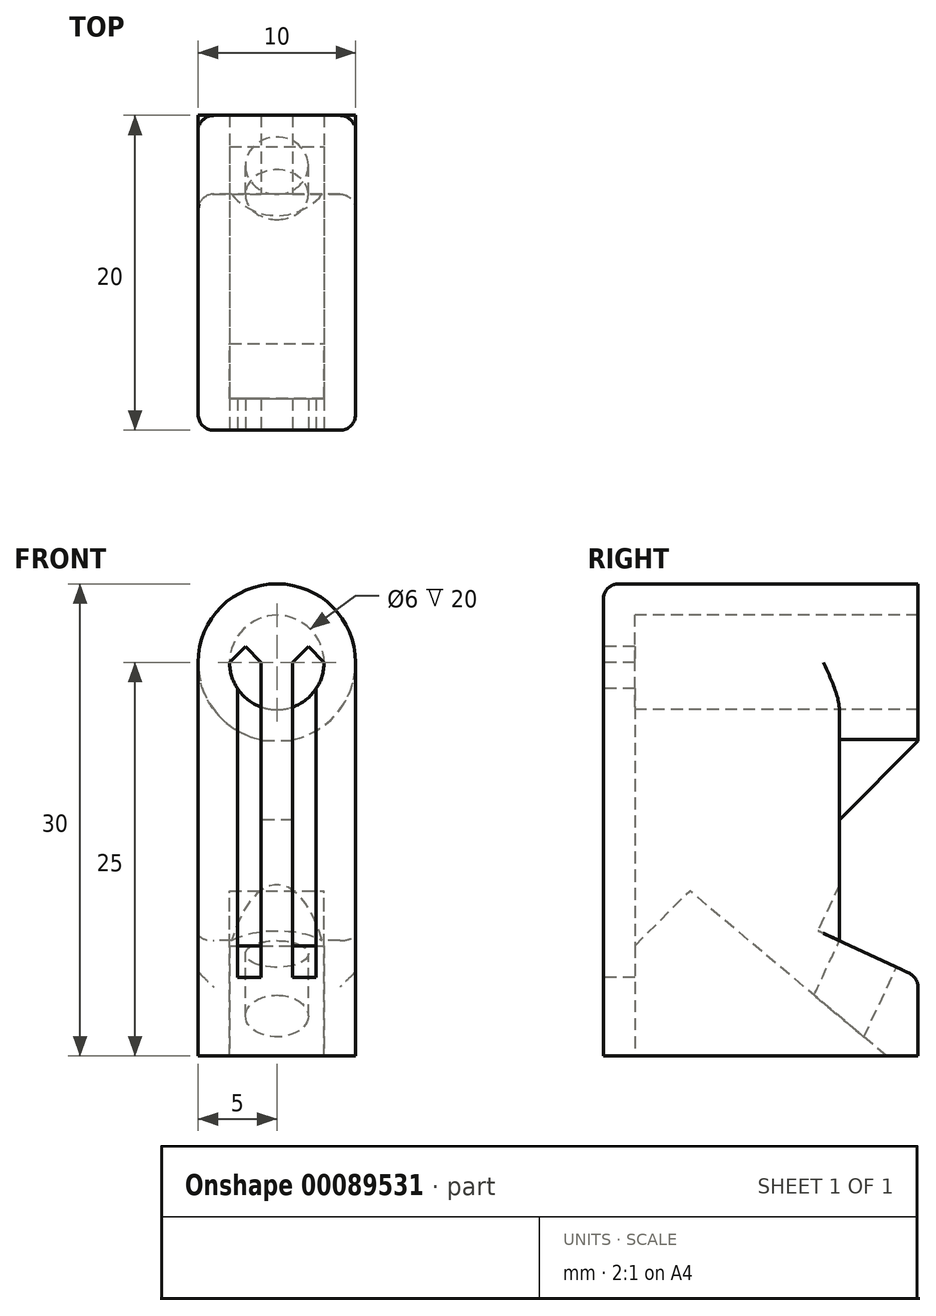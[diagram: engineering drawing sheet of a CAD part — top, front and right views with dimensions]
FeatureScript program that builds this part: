
annotation { "Feature Type Name" : "Feature", "Feature Type Description" : "" }
export const myFeature = defineFeature(function(context is Context, id is Id, definition is map)
    precondition{}
    {
        {
            var Q0;
            Q0=qCreatedBy(makeId("Top.planeOp"),FACE);
            var sketch = newSketch(context, id + "F0", { "sketchPlane" : qUnion([Q0])});
            skLineSegment(sketch, "E0.top", {"start": v(5, 12.5) * mm, "end": v(-5, 12.5) * mm});
            skLineSegment(sketch, "E0.left", {"start": v(5, 7.5) * mm, "end": v(5, 12.5) * mm});
            skLineSegment(sketch, "E0.right", {"start": v(-5, 7.5) * mm, "end": v(-5, 12.5) * mm});
            skLineSegment(sketch, "E1.bottom", {"start": v(5, -7.5) * mm, "end": v(-5, -7.5) * mm});
            skLineSegment(sketch, "E1.top", {"start": v(5, 7.5) * mm, "end": v(-5, 7.5) * mm});
            skLineSegment(sketch, "E1.left", {"start": v(5, -7.5) * mm, "end": v(5, 7.5) * mm});
            skLineSegment(sketch, "E1.right", {"start": v(-5, -7.5) * mm, "end": v(-5, 7.5) * mm});
            skSolve(sketch);
        }
        {
            var Q0;
            Q0=makeQuery(id+"F0.imprint","IMPRINT",FACE,{"disambiguationData":[TD([[makeQuery(id+"F0.imprint","IMPRINT",EDGE,{"derivedFrom":sQuery(id+"F0.wireOp",EDGE,"E1.bottom")}),-1.0]])]});
            extrude(context, id + "F1", {"entities" : qUnion([Q0]), "depth" : 30 * mm});
        }
        {
            var Q0;
            Q0 = qSketchRegion(id + "F0", true);
            extrude(context, id + "F2", {"entities" : qUnion([Q0]), "operationType" : NewBodyOperationType.ADD, "depth" : 5 * mm});
        }
        {
            var Q0;
            Q0=makeQuery(id+"F1.opExtrude","SWEPT_FACE",FACE,{"disambiguationData":[OSD([sQuery(id+"F0.wireOp",EDGE,"E1.bottom")])]});
            var sketch = newSketch(context, id + "F3", { "sketchPlane" : qUnion([Q0])});
            skCircle(sketch, "E2", {"center": v(0, 25) * mm, "radius": 3 * mm});
            skSolve(sketch);
        }
        {
            var Q0;
            Q0 = qSketchRegion(id + "F3", true);
            extrude(context, id + "F4", {"entities" : qUnion([Q0]), "operationType" : NewBodyOperationType.REMOVE, "endBound" : BoundingType.THROUGH_ALL, "oppositeDirection" : true, "depth" : 25 * mm});
        }
        {
            var Q0;
            Q0=makeQuery(id+"F1.opExtrude","SWEPT_FACE",FACE,{"disambiguationData":[OSD([sQuery(id+"F0.wireOp",EDGE,"E1.bottom")])]});
            var sketch = newSketch(context, id + "F5", { "sketchPlane" : qUnion([Q0])});
            skCircle(sketch, "E3.0", {"center": v(0, 25) * mm, "radius": 3 * mm});
            skLineSegment(sketch, "E4", {"start": v(-2.83, 26) * mm, "end": v(2.83, 26) * mm});
            skSolve(sketch);
        }
        {
            var Q0;
            {var subQ0=sQuery(id+"F5.wireOp",EDGE,"E4");Q0=makeQuery(id+"F5.imprint","IMPRINT",FACE,{"disambiguationData":[TD([[makeQuery(id+"F5.imprint","IMPRINT",EDGE,{"derivedFrom":subQ0}),1.0]])]});}
            extrude(context, id + "F6", {"entities" : qUnion([Q0]), "operationType" : NewBodyOperationType.ADD, "oppositeDirection" : true, "depth" : 2 * mm});
        }
        {
            var Q0;
            Q0=makeQuery(id+"F2.opExtrude","CAP_FACE",FACE,{"disambiguationData":[OSD([sQuery(id+"F0.wireOp",EDGE,"E0.bottom"),sQuery(id+"F0.wireOp",EDGE,"E0.top"),sQuery(id+"F0.wireOp",EDGE,"E0.left"),sQuery(id+"F0.wireOp",EDGE,"E0.right"),sQuery(id+"F0.wireOp",EDGE,"E1.bottom"),sQuery(id+"F0.wireOp",EDGE,"E1.top"),sQuery(id+"F0.wireOp",EDGE,"E1.left"),sQuery(id+"F0.wireOp",EDGE,"E1.right")])],"isStart":false});
            var sketch = newSketch(context, id + "F7", { "sketchPlane" : qUnion([Q0])});
            skLineSegment(sketch, "E5.bottom", {"start": v(-1, -7.5) * mm, "end": v(-2.5, -7.5) * mm});
            skLineSegment(sketch, "E5.top", {"start": v(-1, -5.5) * mm, "end": v(-2.5, -5.5) * mm});
            skLineSegment(sketch, "E5.left", {"start": v(-1, -7.5) * mm, "end": v(-1, -5.5) * mm});
            skLineSegment(sketch, "E5.right", {"start": v(-2.5, -7.5) * mm, "end": v(-2.5, -5.5) * mm});
            skPoint(sketch, "E5.middle", {"position": v(-1.75, -6.5) * mm});
            skLineSegment(sketch, "E6.bottom", {"start": v(2.5, -5.5) * mm, "end": v(1, -5.5) * mm});
            skLineSegment(sketch, "E6.top", {"start": v(2.5, -7.5) * mm, "end": v(1, -7.5) * mm});
            skLineSegment(sketch, "E6.left", {"start": v(1, -5.5) * mm, "end": v(1, -7.5) * mm});
            skLineSegment(sketch, "E6.right", {"start": v(2.5, -5.5) * mm, "end": v(2.5, -7.5) * mm});
            skPoint(sketch, "E6.middle", {"position": v(1.75, -6.5) * mm});
            skSolve(sketch);
        }
        {
            var Q0;
            Q0 = qSketchRegion(id + "F7", true);
            var Q1;
            Q1=makeQuery(id+"F6.opExtrude","SWEPT_FACE",FACE,{"disambiguationData":[OSD([sQuery(id+"F5.wireOp",EDGE,"E4")])]});
            extrude(context, id + "F8", {"entities" : qUnion([Q0]), "operationType" : NewBodyOperationType.REMOVE, "endBound" : BoundingType.UP_TO_SURFACE, "endBoundEntityFace" : qUnion([Q1]), "depth" : 25 * mm});
        }
        {
            var Q0;
            Q0=makeQuery(id+"F8.boolean.opBoolean","MERGE",FACE,{"derivedFrom":[makeQuery(id+"F6.opExtrude","SWEPT_FACE",FACE,{"disambiguationData":[OSD([sQuery(id+"F5.wireOp",EDGE,"E4")])]}),makeQuery(id+"F8.opExtrude","CAP_FACE",FACE,{"disambiguationData":[OSD([sQuery(id+"F7.wireOp",EDGE,"E5.bottom"),sQuery(id+"F7.wireOp",EDGE,"E5.top"),sQuery(id+"F7.wireOp",EDGE,"E5.left"),sQuery(id+"F7.wireOp",EDGE,"E5.right")])],"isStart":false}),makeQuery(id+"F8.opExtrude","CAP_FACE",FACE,{"disambiguationData":[OSD([sQuery(id+"F7.wireOp",EDGE,"E6.bottom"),sQuery(id+"F7.wireOp",EDGE,"E6.top"),sQuery(id+"F7.wireOp",EDGE,"E6.left"),sQuery(id+"F7.wireOp",EDGE,"E6.right")])],"isStart":false})]});
            var sketch = newSketch(context, id + "F9", { "sketchPlane" : qUnion([Q0])});
            skLineSegment(sketch, "E7.0", {"start": v(-1, 7.5) * mm, "end": v(-1, 5.5) * mm});
            skLineSegment(sketch, "E8.0", {"start": v(1, 5.5) * mm, "end": v(1, 7.5) * mm});
            skLineSegment(sketch, "E9.0", {"start": v(-1, 7.5) * mm, "end": v(1, 7.5) * mm});
            skLineSegment(sketch, "E10", {"start": v(-1, 5.5) * mm, "end": v(1, 5.5) * mm});
            skSolve(sketch);
        }
        {
            var Q0;
            Q0 = qSketchRegion(id + "F9", true);
            var Q1;
            Q1=makeQuery(id+"F4.boolean.opBoolean","COPY",FACE,{"derivedFrom":makeQuery(id+"F4.opExtrude","SWEPT_FACE",FACE,{"disambiguationData":[OSD([sQuery(id+"F3.wireOp",EDGE,"E2")])]})});
            extrude(context, id + "F10", {"entities" : qUnion([Q0]), "operationType" : NewBodyOperationType.ADD, "endBound" : BoundingType.UP_TO_SURFACE, "endBoundEntityFace" : qUnion([Q1]), "depth" : 25 * mm});
        }
        {
            var Q0;
            {var subQ0=sQuery(id+"F0.wireOp",EDGE,"E1.right");var subQ1=sQuery(id+"F0.wireOp",EDGE,"E1.left");var subQ2=sQuery(id+"F0.wireOp",EDGE,"E1.bottom");Q0=makeQuery(id+"F2.boolean.opBoolean","MERGE",FACE,{"derivedFrom":[makeQuery(id+"F1.opExtrude","CAP_FACE",FACE,{"disambiguationData":[OSD([subQ2,sQuery(id+"F0.wireOp",EDGE,"E1.top"),subQ1,subQ0])],"isStart":true}),makeQuery(id+"F2.opExtrude","CAP_FACE",FACE,{"disambiguationData":[OSD([sQuery(id+"F0.wireOp",EDGE,"E0.top"),sQuery(id+"F0.wireOp",EDGE,"E0.left"),sQuery(id+"F0.wireOp",EDGE,"E0.right"),subQ2,subQ1,subQ0])],"isStart":true})]});}
            var sketch = newSketch(context, id + "F11", { "sketchPlane" : qUnion([Q0])});
            skLineSegment(sketch, "E11.0", {"start": v(5, -12.5) * mm, "end": v(-5, -12.5) * mm});
            skLineSegment(sketch, "E12", {"start": v(-5, -12.5) * mm, "end": v(-5, -10.5) * mm});
            skLineSegment(sketch, "E13", {"start": v(-5, -10.5) * mm, "end": v(5, -10.5) * mm});
            skLineSegment(sketch, "E14", {"start": v(5, -10.5) * mm, "end": v(5, -12.5) * mm});
            skLineSegment(sketch, "E15.0", {"start": v(5, 7.5) * mm, "end": v(-5, 7.5) * mm});
            skLineSegment(sketch, "E16", {"start": v(-5, 7.5) * mm, "end": v(-5, 5.5) * mm});
            skLineSegment(sketch, "E17", {"start": v(-5, 5.5) * mm, "end": v(5, 5.5) * mm});
            skLineSegment(sketch, "E18", {"start": v(5, 5.5) * mm, "end": v(5, 7.5) * mm});
            skSolve(sketch);
        }
        {
            var Q0;
            {var subQ0=sQuery(id+"F0.wireOp",EDGE,"E1.right");Q0=makeQuery(id+"F3h623T3k0yUvjH_1.boolean.opBoolean","MERGE",FACE,{"derivedFrom":[makeQuery(id+"F2.boolean.opBoolean","MERGE",FACE,{"derivedFrom":[makeQuery(id+"F1.opExtrude","SWEPT_FACE",FACE,{"disambiguationData":[OSD([subQ0])]}),makeQuery(id+"F2.opExtrude","SWEPT_FACE",FACE,{"disambiguationData":[OSD([sQuery(id+"F0.wireOp",EDGE,"E0.right"),subQ0])]})]}),makeQuery(id+"F3h623T3k0yUvjH_1.opExtrude","SWEPT_FACE",FACE,{"disambiguationData":[OSD([sQuery(id+"F11.wireOp",EDGE,"E12")])]}),makeQuery(id+"F3h623T3k0yUvjH_1.opExtrude","SWEPT_FACE",FACE,{"disambiguationData":[OSD([sQuery(id+"F11.wireOp",EDGE,"E16")])]})]});}
            var sketch = newSketch(context, id + "F12", { "sketchPlane" : qUnion([Q0])});
            skLineSegment(sketch, "E19", {"start": v(-12.5, 5) * mm, "end": v(-7.5, 7.33) * mm});
            skLineSegment(sketch, "E20", {"start": v(-7.5, 7.33) * mm, "end": v(-7.5, 5) * mm});
            skLineSegment(sketch, "E21", {"start": v(-7.5, 5) * mm, "end": v(-12.5, 5) * mm});
            skSolve(sketch);
        }
        {
            var Q0;
            Q0 = qSketchRegion(id + "F12", true);
            var Q1;
            {var subQ0=sQuery(id+"F0.wireOp",EDGE,"E1.left");Q1=makeQuery(id+"F3h623T3k0yUvjH_1.boolean.opBoolean","MERGE",FACE,{"derivedFrom":[makeQuery(id+"F2.boolean.opBoolean","MERGE",FACE,{"derivedFrom":[makeQuery(id+"F1.opExtrude","SWEPT_FACE",FACE,{"disambiguationData":[OSD([subQ0])]}),makeQuery(id+"F2.opExtrude","SWEPT_FACE",FACE,{"disambiguationData":[OSD([sQuery(id+"F0.wireOp",EDGE,"E0.left"),subQ0])]})]}),makeQuery(id+"F3h623T3k0yUvjH_1.opExtrude","SWEPT_FACE",FACE,{"disambiguationData":[OSD([sQuery(id+"F11.wireOp",EDGE,"E14")])]}),makeQuery(id+"F3h623T3k0yUvjH_1.opExtrude","SWEPT_FACE",FACE,{"disambiguationData":[OSD([sQuery(id+"F11.wireOp",EDGE,"E18")])]})]});}
            extrude(context, id + "F13", {"entities" : qUnion([Q0]), "operationType" : NewBodyOperationType.ADD, "endBound" : BoundingType.UP_TO_SURFACE, "oppositeDirection" : true, "endBoundEntityFace" : qUnion([Q1]), "depth" : 25 * mm});
        }
        {
            var Q0;
            Q0=makeQuery(id+"F13.opExtrude","SWEPT_FACE",FACE,{"disambiguationData":[OSD([sQuery(id+"F12.wireOp",EDGE,"E19")])]});
            var sketch = newSketch(context, id + "F14", { "sketchPlane" : qUnion([Q0])});
            skCircle(sketch, "E22", {"center": v(0, 5.7) * mm, "radius": 2 * mm});
            skSolve(sketch);
        }
        {
            var Q0;
            Q0 = qSketchRegion(id + "F14", true);
            extrude(context, id + "F15", {"entities" : qUnion([Q0]), "operationType" : NewBodyOperationType.REMOVE, "endBound" : BoundingType.THROUGH_ALL, "oppositeDirection" : true, "depth" : 25 * mm});
        }
        {
            var Q0;
            Q0=makeQuery(id+"F13.opExtrude","SWEPT_FACE",FACE,{"disambiguationData":[OSD([sQuery(id+"F12.wireOp",EDGE,"E19")])]});
            var sketch = newSketch(context, id + "F16", { "sketchPlane" : qUnion([Q0])});
            skCircle(sketch, "E23", {"center": v(0, 5.7) * mm, "radius": 3.5 * mm});
            skSolve(sketch);
        }
        {
            var Q0;
            Q0 = qSketchRegion(id + "F16", true);
            extrude(context, id + "F17", {"entities" : qUnion([Q0]), "operationType" : NewBodyOperationType.REMOVE, "endBound" : BoundingType.THROUGH_ALL, "depth" : 25 * mm});
        }
        {
            var Q0;
            Q0=makeQuery(id+"F1.opExtrude","CAP_EDGE",EDGE,{"disambiguationData":[OSD([sQuery(id+"F0.wireOp",EDGE,"E1.left")])],"isStart":false});
            var Q1;
            Q1=makeQuery(id+"F1.opExtrude","CAP_EDGE",EDGE,{"disambiguationData":[OSD([sQuery(id+"F0.wireOp",EDGE,"E1.right")])],"isStart":false});
            fillet(context, id + "F18", {"entities" : qUnion([Q0, Q1]), "radius" : 5 * mm, "tangentPropagation" : true, "allowEdgeOverflow" : false});
        }
        {
            var Q0;
            Q0=makeQuery(id+"F1.opExtrude","SWEPT_FACE",FACE,{"disambiguationData":[OSD([sQuery(id+"F0.wireOp",EDGE,"E1.top")])]});
            var sketch = newSketch(context, id + "F19", { "sketchPlane" : qUnion([Q0])});
            skCircle(sketch, "E24", {"center": v(0, 25) * mm, "radius": 5 * mm});
            skCircle(sketch, "E25.0", {"center": v(0, 25) * mm, "radius": 3 * mm});
            skSolve(sketch);
        }
        {
            var Q0;
            Q0 = qSketchRegion(id + "F19", true);
            extrude(context, id + "F20", {"entities" : qUnion([Q0]), "operationType" : NewBodyOperationType.ADD, "depth" : 5 * mm});
        }
        {
            var Q0;
            Q0=makeQuery(id+"F2.opExtrude","CAP_EDGE",EDGE,{"disambiguationData":[OSD([sQuery(id+"F0.wireOp",EDGE,"E0.top")])],"isStart":false});
            var Q1;
            Q1=makeQuery(id+"F3h623T3k0yUvjH_1.boolean.opBoolean","MERGE",EDGE,{"derivedFrom":[makeQuery(id+"F2.opExtrude","SWEPT_EDGE",EDGE,{"disambiguationData":[OSD([sQuery(id+"F0.wireOp",EDGE,"E0.top"),sQuery(id+"F0.wireOp",EDGE,"E0.left")])]}),makeQuery(id+"F3h623T3k0yUvjH_1.opExtrude","SWEPT_EDGE",EDGE,{"disambiguationData":[OSD([sQuery(id+"F11.wireOp",EDGE,"E11.0"),sQuery(id+"F11.wireOp",EDGE,"E14")])]})]});
            var Q2;
            Q2=makeQuery(id+"F3h623T3k0yUvjH_1.boolean.opBoolean","MERGE",EDGE,{"derivedFrom":[makeQuery(id+"F2.opExtrude","SWEPT_EDGE",EDGE,{"disambiguationData":[OSD([sQuery(id+"F0.wireOp",EDGE,"E0.top"),sQuery(id+"F0.wireOp",EDGE,"E0.right")])]}),makeQuery(id+"F3h623T3k0yUvjH_1.opExtrude","SWEPT_EDGE",EDGE,{"disambiguationData":[OSD([sQuery(id+"F11.wireOp",EDGE,"E11.0"),sQuery(id+"F11.wireOp",EDGE,"E12")])]})]});
            var Q3;
            Q3=makeQuery(id+"F2.opExtrude","CAP_EDGE",EDGE,{"disambiguationData":[OSD([sQuery(id+"F0.wireOp",EDGE,"E0.left"),sQuery(id+"F0.wireOp",EDGE,"E1.left")])],"isStart":false});
            var Q4;
            Q4=makeQuery(id+"F1.opExtrude","SWEPT_EDGE",EDGE,{"disambiguationData":[OSD([sQuery(id+"F0.wireOp",EDGE,"E0.left"),sQuery(id+"F0.wireOp",EDGE,"E1.top"),sQuery(id+"F0.wireOp",EDGE,"E1.left")])]});
            var Q5;
            Q5=makeQuery(id+"F1.opExtrude","SWEPT_EDGE",EDGE,{"disambiguationData":[OSD([sQuery(id+"F0.wireOp",EDGE,"E0.right"),sQuery(id+"F0.wireOp",EDGE,"E1.top"),sQuery(id+"F0.wireOp",EDGE,"E1.right")])]});
            var Q6;
            Q6=makeQuery(id+"F3h623T3k0yUvjH_1.boolean.opBoolean","MERGE",EDGE,{"derivedFrom":[makeQuery(id+"F1.opExtrude","SWEPT_EDGE",EDGE,{"disambiguationData":[OSD([sQuery(id+"F0.wireOp",EDGE,"E1.bottom"),sQuery(id+"F0.wireOp",EDGE,"E1.left")])]}),makeQuery(id+"F3h623T3k0yUvjH_1.opExtrude","SWEPT_EDGE",EDGE,{"disambiguationData":[OSD([sQuery(id+"F11.wireOp",EDGE,"E15.0"),sQuery(id+"F11.wireOp",EDGE,"E18")])]})]});
            var Q7;
            Q7=makeQuery(id+"F3h623T3k0yUvjH_1.boolean.opBoolean","MERGE",EDGE,{"derivedFrom":[makeQuery(id+"F1.opExtrude","SWEPT_EDGE",EDGE,{"disambiguationData":[OSD([sQuery(id+"F0.wireOp",EDGE,"E1.bottom"),sQuery(id+"F0.wireOp",EDGE,"E1.right")])]}),makeQuery(id+"F3h623T3k0yUvjH_1.opExtrude","SWEPT_EDGE",EDGE,{"disambiguationData":[OSD([sQuery(id+"F11.wireOp",EDGE,"E15.0"),sQuery(id+"F11.wireOp",EDGE,"E16")])]})]});
            var Q8;
            Q8=makeQuery(id+"F2.opExtrude","CAP_EDGE",EDGE,{"disambiguationData":[OSD([sQuery(id+"F0.wireOp",EDGE,"E0.right"),sQuery(id+"F0.wireOp",EDGE,"E1.right")])],"isStart":false});
            fillet(context, id + "F21", {"entities" : qUnion([Q0, Q1, Q2, Q3, Q4, Q5, Q6, Q7, Q8]), "radius" : 1 * mm, "tangentPropagation" : true, "allowEdgeOverflow" : false});
        }
        {
            var Q0;
            Q0=qCreatedBy(makeId("Right.planeOp"),FACE);
            var sketch = newSketch(context, id + "F22", { "sketchPlane" : qUnion([Q0])});
            skLineSegment(sketch, "E26", {"start": v(10.5, 0) * mm, "end": v(-2, 10.5) * mm});
            skLineSegment(sketch, "E27", {"start": v(-5.5, 7) * mm, "end": v(-5.5, 0) * mm});
            skLineSegment(sketch, "E28", {"start": v(10.5, 0) * mm, "end": v(-5.5, 0) * mm});
            skLineSegment(sketch, "E29", {"start": v(-5.5, 7) * mm, "end": v(-2, 10.5) * mm});
            skSolve(sketch);
        }
        {
            var Q0;
            Q0 = qSketchRegion(id + "F22", true);
            extrude(context, id + "F23", {"entities" : qUnion([Q0]), "operationType" : NewBodyOperationType.REMOVE, "oppositeDirection" : true, "depth" : 3 * mm, "hasSecondDirection" : true, "secondDirectionOppositeDirection" : false, "secondDirectionDepth" : 3 * mm});
        }
        {
            var Q0;
            Q0=qCreatedBy(makeId("Right.planeOp"),FACE);
            var sketch = newSketch(context, id + "F24", { "sketchPlane" : qUnion([Q0])});
            skLineSegment(sketch, "E30", {"start": v(12.5, 20) * mm, "end": v(7.5, 20) * mm});
            skLineSegment(sketch, "E31", {"start": v(7.5, 20) * mm, "end": v(7.5, 15) * mm});
            skLineSegment(sketch, "E32", {"start": v(7.5, 15) * mm, "end": v(12.5, 20) * mm});
            skLineSegment(sketch, "E33.0", {"start": v(12.5, 30) * mm, "end": v(12.5, 20) * mm, "construction": true});
            skLineSegment(sketch, "E34", {"start": v(12.5, 20) * mm, "end": v(12.5, 22) * mm});
            skLineSegment(sketch, "E35", {"start": v(12.5, 22) * mm, "end": v(7.5, 22) * mm});
            skLineSegment(sketch, "E36", {"start": v(7.5, 22) * mm, "end": v(7.5, 20) * mm});
            skSolve(sketch);
        }
        {
            var Q0;
            Q0 = qSketchRegion(id + "F24", true);
            extrude(context, id + "F25", {"entities" : qUnion([Q0]), "operationType" : NewBodyOperationType.ADD, "depth" : 1 * mm, "hasSecondDirection" : true, "secondDirectionOppositeDirection" : true, "secondDirectionDepth" : 1 * mm});
        }
        {
            var Q0;
            Q0=makeQuery(id+"F10.boolean.opBoolean","MERGE",FACE,{"derivedFrom":[makeQuery(id+"F6.boolean.opBoolean","MERGE",FACE,{"derivedFrom":[makeQuery(id+"F1.opExtrude","SWEPT_FACE",FACE,{"disambiguationData":[OSD([sQuery(id+"F0.wireOp",EDGE,"E1.bottom")])]}),makeQuery(id+"F6.opExtrude","CAP_FACE",FACE,{"disambiguationData":[OSD([sQuery(id+"F5.wireOp",EDGE,"E3.0"),sQuery(id+"F5.wireOp",EDGE,"E4")])],"isStart":true})]}),makeQuery(id+"F10.opExtrude","SWEPT_FACE",FACE,{"disambiguationData":[OSD([sQuery(id+"F9.wireOp",EDGE,"E9.0")])]})]});
            var sketch = newSketch(context, id + "F26", { "sketchPlane" : qUnion([Q0])});
            skLineSegment(sketch, "E37", {"start": v(-3, 26) * mm, "end": v(-1, 26) * mm});
            skLineSegment(sketch, "E38", {"start": v(-1, 26) * mm, "end": v(-1, 25) * mm});
            skLineSegment(sketch, "E39", {"start": v(-1, 25) * mm, "end": v(-2, 26) * mm});
            skLineSegment(sketch, "E40", {"start": v(-2, 26) * mm, "end": v(-3, 25) * mm});
            skLineSegment(sketch, "E41", {"start": v(-3, 25) * mm, "end": v(-3, 26) * mm});
            skLineSegment(sketch, "E42.MirrorCS", {"start": v(3, 26) * mm, "end": v(1, 26) * mm});
            skLineSegment(sketch, "E43.MirrorCS", {"start": v(1, 26) * mm, "end": v(1, 25) * mm});
            skLineSegment(sketch, "E44.MirrorCS", {"start": v(2, 26) * mm, "end": v(3, 25) * mm});
            skLineSegment(sketch, "E45.MirrorCS", {"start": v(3, 25) * mm, "end": v(3, 26) * mm});
            skLineSegment(sketch, "E46.MirrorCS", {"start": v(1, 25) * mm, "end": v(2, 26) * mm});
            skSolve(sketch);
        }
        {
            var Q0;
            Q0 = qSketchRegion(id + "F26", true);
            extrude(context, id + "F27", {"entities" : qUnion([Q0]), "operationType" : NewBodyOperationType.ADD, "oppositeDirection" : true, "depth" : 2 * mm});
        }
    });
